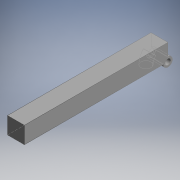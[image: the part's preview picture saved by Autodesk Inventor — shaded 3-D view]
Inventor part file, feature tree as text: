
AUTODESK INVENTOR PART (.ipt)
format: ipt  version: 2018 (Build 220112000, 112)  size: 133,632 bytes
history: native  units: in
note: dims shown in document units (in); Inventor stores cm internally (conversion verified against a paired STEP export)
features: extrude x3, sweep x3, other x1, plane x1, imported_body x1
ambient origin geometry x8: Origin, YZ Plane, XZ Plane, XY Plane, X Axis, Y Axis, Z Axis, Center Point
bodies: Solid1 (feature_tree)
feature tree (9):
  extrude  "Main Body"  TaperAngle=0.0deg  [1 undecoded]
  other  "Hinge Sketch"
  extrude  "Hinge Surround"  Depth=0.1339in
  extrude  "Hinge Hole"  Depth=0.0394in
  plane  "Work Plane1"
  sweep  "Sweep2"
  imported_body  "Base"
  sweep  "Sweep Path"
  sweep  "Sweep Profile"
note: 1 required parameter value undecoded (feature->parameter linkage not recoverable at this tier; creation-order binding heuristic only, values carry confidence <= 0.55)
